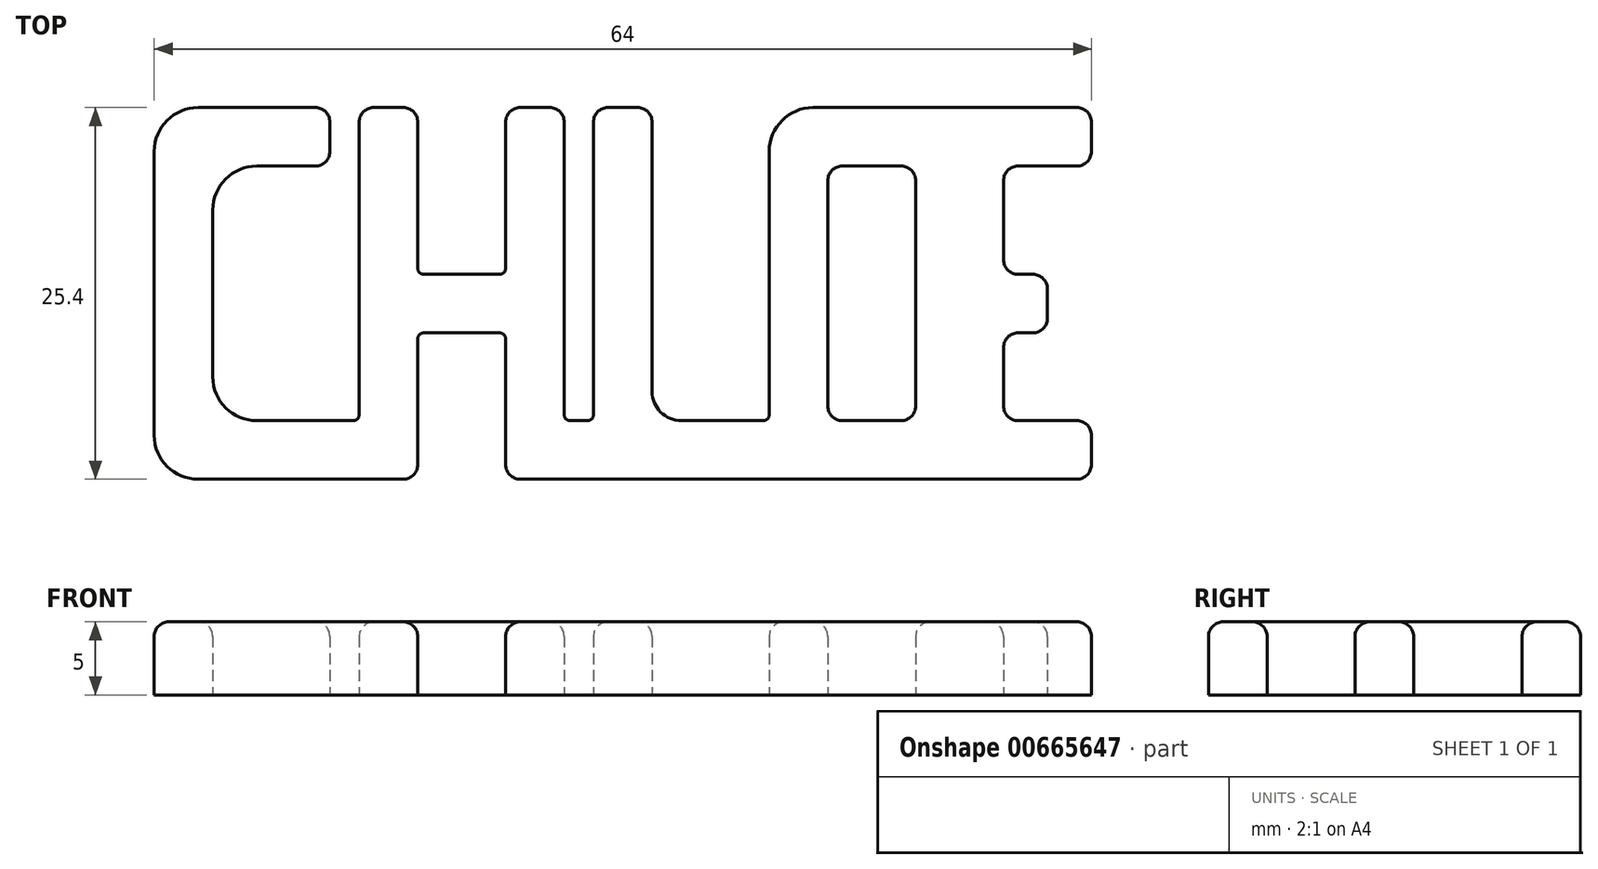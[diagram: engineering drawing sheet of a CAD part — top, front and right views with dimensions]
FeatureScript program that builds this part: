
annotation { "Feature Type Name" : "Feature", "Feature Type Description" : "" }
export const myFeature = defineFeature(function(context is Context, id is Id, definition is map)
    precondition{}
    {
        {
            var Q0;
            Q0=qCreatedBy(makeId("Top.planeOp"),FACE);
            var sketch = newSketch(context, id + "F0", { "sketchPlane" : qUnion([Q0])});
            skLineSegment(sketch, "E0", {"start": v(0, 0) * mm, "end": v(0, 25.4) * mm});
            skLineSegment(sketch, "E1", {"start": v(0, 25.4) * mm, "end": v(12, 25.4) * mm});
            skLineSegment(sketch, "E2", {"start": v(12, 25.4) * mm, "end": v(12, 21.4) * mm});
            skLineSegment(sketch, "E3", {"start": v(12, 21.4) * mm, "end": v(4, 21.4) * mm});
            skLineSegment(sketch, "E4", {"start": v(4, 21.4) * mm, "end": v(4, 4) * mm});
            skLineSegment(sketch, "E5", {"start": v(4, 4) * mm, "end": v(14, 4) * mm});
            skLineSegment(sketch, "E6", {"start": v(14, 4) * mm, "end": v(14, 25.4) * mm});
            skLineSegment(sketch, "E7", {"start": v(14, 25.4) * mm, "end": v(18, 25.4) * mm});
            skLineSegment(sketch, "E8", {"start": v(18, 25.4) * mm, "end": v(18, 14) * mm});
            skLineSegment(sketch, "E9", {"start": v(18, 14) * mm, "end": v(24, 14) * mm});
            skLineSegment(sketch, "E10", {"start": v(24, 14) * mm, "end": v(24, 25.4) * mm});
            skLineSegment(sketch, "E11", {"start": v(24, 25.4) * mm, "end": v(28, 25.4) * mm});
            skLineSegment(sketch, "E12", {"start": v(34, 4) * mm, "end": v(42, 4) * mm});
            skLineSegment(sketch, "E13", {"start": v(42, 4) * mm, "end": v(42, 25.4) * mm});
            skLineSegment(sketch, "E14", {"start": v(42, 25.4) * mm, "end": v(64, 25.4) * mm});
            skLineSegment(sketch, "E15", {"start": v(64, 25.4) * mm, "end": v(64, 21.4) * mm});
            skLineSegment(sketch, "E16", {"start": v(64, 21.4) * mm, "end": v(58, 21.4) * mm});
            skLineSegment(sketch, "E17", {"start": v(58, 21.4) * mm, "end": v(58, 14) * mm});
            skLineSegment(sketch, "E18", {"start": v(58, 14) * mm, "end": v(61, 14) * mm});
            skLineSegment(sketch, "E19", {"start": v(61, 14) * mm, "end": v(61, 10) * mm});
            skLineSegment(sketch, "E20", {"start": v(61, 10) * mm, "end": v(58, 10) * mm});
            skLineSegment(sketch, "E21", {"start": v(58, 10) * mm, "end": v(58, 4) * mm});
            skLineSegment(sketch, "E22", {"start": v(58, 4) * mm, "end": v(64, 4) * mm});
            skLineSegment(sketch, "E23", {"start": v(64, 4) * mm, "end": v(64, 0) * mm});
            skLineSegment(sketch, "E24", {"start": v(64, 0) * mm, "end": v(24, 0) * mm});
            skLineSegment(sketch, "E25", {"start": v(18, 0) * mm, "end": v(18, 10) * mm});
            skLineSegment(sketch, "E26", {"start": v(18, 10) * mm, "end": v(24, 10) * mm});
            skLineSegment(sketch, "E27", {"start": v(24, 10) * mm, "end": v(24, 0) * mm});
            skLineSegment(sketch, "E28.trimOffspring", {"start": v(18, 0) * mm, "end": v(0, 0) * mm});
            skLineSegment(sketch, "E29.bottom", {"start": v(46, 21.4) * mm, "end": v(52, 21.4) * mm});
            skLineSegment(sketch, "E29.top", {"start": v(46, 4) * mm, "end": v(52, 4) * mm});
            skLineSegment(sketch, "E29.left", {"start": v(46, 21.4) * mm, "end": v(46, 4) * mm});
            skLineSegment(sketch, "E29.right", {"start": v(52, 21.4) * mm, "end": v(52, 4) * mm});
            skLineSegment(sketch, "E30", {"start": v(28, 25.4) * mm, "end": v(28, 4) * mm});
            skLineSegment(sketch, "E31", {"start": v(28, 4) * mm, "end": v(30, 4) * mm});
            skLineSegment(sketch, "E32", {"start": v(30, 4) * mm, "end": v(30, 25.4) * mm});
            skLineSegment(sketch, "E33", {"start": v(30, 25.4) * mm, "end": v(34, 25.4) * mm});
            skLineSegment(sketch, "E34", {"start": v(34, 25.4) * mm, "end": v(34, 4) * mm});
            skSolve(sketch);
        }
        {
            var Q0;
            Q0=makeQuery(id+"F0.imprint","IMPRINT",FACE,{"disambiguationData":[TD([[makeQuery(id+"F0.imprint","IMPRINT",EDGE,{"derivedFrom":sQuery(id+"F0.wireOp",EDGE,"E0")}),-1.0]])]});
            extrude(context, id + "F1", {"entities" : qUnion([Q0]), "depth" : 5 * mm, "offsetDistance" : 25 * mm});
        }
        {
            var Q0;
            Q0=makeQuery(id+"F1.opExtrude","SWEPT_EDGE",EDGE,{"disambiguationData":[OSD([sQuery(id+"F0.wireOp",EDGE,"E1"),sQuery(id+"F0.wireOp",EDGE,"E2")])]});
            var Q1;
            Q1=makeQuery(id+"F1.opExtrude","SWEPT_EDGE",EDGE,{"disambiguationData":[OSD([sQuery(id+"F0.wireOp",EDGE,"E2"),sQuery(id+"F0.wireOp",EDGE,"E3")])]});
            var Q2;
            Q2=makeQuery(id+"F1.opExtrude","SWEPT_EDGE",EDGE,{"disambiguationData":[OSD([sQuery(id+"F0.wireOp",EDGE,"E6"),sQuery(id+"F0.wireOp",EDGE,"E7")])]});
            var Q3;
            Q3=makeQuery(id+"F1.opExtrude","SWEPT_EDGE",EDGE,{"disambiguationData":[OSD([sQuery(id+"F0.wireOp",EDGE,"E7"),sQuery(id+"F0.wireOp",EDGE,"E8")])]});
            var Q4;
            Q4=makeQuery(id+"F1.opExtrude","SWEPT_EDGE",EDGE,{"disambiguationData":[OSD([sQuery(id+"F0.wireOp",EDGE,"E10"),sQuery(id+"F0.wireOp",EDGE,"E11")])]});
            var Q5;
            Q5=makeQuery(id+"F1.opExtrude","SWEPT_EDGE",EDGE,{"disambiguationData":[OSD([sQuery(id+"F0.wireOp",EDGE,"E11"),sQuery(id+"F0.wireOp",EDGE,"E30")])]});
            var Q6;
            Q6=makeQuery(id+"F1.opExtrude","SWEPT_EDGE",EDGE,{"disambiguationData":[OSD([sQuery(id+"F0.wireOp",EDGE,"E32"),sQuery(id+"F0.wireOp",EDGE,"E33")])]});
            var Q7;
            Q7=makeQuery(id+"F1.opExtrude","SWEPT_EDGE",EDGE,{"disambiguationData":[OSD([sQuery(id+"F0.wireOp",EDGE,"E33"),sQuery(id+"F0.wireOp",EDGE,"E34")])]});
            var Q8;
            Q8=makeQuery(id+"F1.opExtrude","SWEPT_EDGE",EDGE,{"disambiguationData":[OSD([sQuery(id+"F0.wireOp",EDGE,"E14"),sQuery(id+"F0.wireOp",EDGE,"E15")])]});
            var Q9;
            Q9=makeQuery(id+"F1.opExtrude","SWEPT_EDGE",EDGE,{"disambiguationData":[OSD([sQuery(id+"F0.wireOp",EDGE,"E15"),sQuery(id+"F0.wireOp",EDGE,"E16")])]});
            var Q10;
            Q10=makeQuery(id+"F1.opExtrude","SWEPT_EDGE",EDGE,{"disambiguationData":[OSD([sQuery(id+"F0.wireOp",EDGE,"E18"),sQuery(id+"F0.wireOp",EDGE,"E19")])]});
            var Q11;
            Q11=makeQuery(id+"F1.opExtrude","SWEPT_EDGE",EDGE,{"disambiguationData":[OSD([sQuery(id+"F0.wireOp",EDGE,"E19"),sQuery(id+"F0.wireOp",EDGE,"E20")])]});
            var Q12;
            Q12=makeQuery(id+"F1.opExtrude","SWEPT_EDGE",EDGE,{"disambiguationData":[OSD([sQuery(id+"F0.wireOp",EDGE,"E22"),sQuery(id+"F0.wireOp",EDGE,"E23")])]});
            var Q13;
            Q13=makeQuery(id+"F1.opExtrude","SWEPT_EDGE",EDGE,{"disambiguationData":[OSD([sQuery(id+"F0.wireOp",EDGE,"E23"),sQuery(id+"F0.wireOp",EDGE,"E24")])]});
            var Q14;
            Q14=makeQuery(id+"F1.opExtrude","SWEPT_EDGE",EDGE,{"disambiguationData":[OSD([sQuery(id+"F0.wireOp",EDGE,"E25"),sQuery(id+"F0.wireOp",EDGE,"E28.trimOffspring")])]});
            var Q15;
            Q15=makeQuery(id+"F1.opExtrude","SWEPT_EDGE",EDGE,{"disambiguationData":[OSD([sQuery(id+"F0.wireOp",EDGE,"E24"),sQuery(id+"F0.wireOp",EDGE,"E27")])]});
            var Q16;
            Q16=makeQuery(id+"F1.opExtrude","SWEPT_EDGE",EDGE,{"disambiguationData":[OSD([sQuery(id+"F0.wireOp",EDGE,"E29.bottom"),sQuery(id+"F0.wireOp",EDGE,"E29.left")])]});
            var Q17;
            Q17=makeQuery(id+"F1.opExtrude","SWEPT_EDGE",EDGE,{"disambiguationData":[OSD([sQuery(id+"F0.wireOp",EDGE,"E29.bottom"),sQuery(id+"F0.wireOp",EDGE,"E29.right")])]});
            var Q18;
            Q18=makeQuery(id+"F1.opExtrude","SWEPT_EDGE",EDGE,{"disambiguationData":[OSD([sQuery(id+"F0.wireOp",EDGE,"E29.top"),sQuery(id+"F0.wireOp",EDGE,"E29.right")])]});
            var Q19;
            Q19=makeQuery(id+"F1.opExtrude","SWEPT_EDGE",EDGE,{"disambiguationData":[OSD([sQuery(id+"F0.wireOp",EDGE,"E29.top"),sQuery(id+"F0.wireOp",EDGE,"E29.left")])]});
            fillet(context, id + "F2", {"entities" : qUnion([Q0, Q1, Q2, Q3, Q4, Q5, Q6, Q7, Q8, Q9, Q10, Q11, Q12, Q13, Q14, Q15, Q16, Q17, Q18, Q19]), "tangentPropagation" : true, "radius" : 1 * mm, "defaultsChanged" : false, "vertexSettings" : [], "allowEdgeOverflow" : false});
        }
        {
            var Q0;
            Q0=makeQuery(id+"F1.opExtrude","SWEPT_EDGE",EDGE,{"disambiguationData":[OSD([sQuery(id+"F0.wireOp",EDGE,"E12"),sQuery(id+"F0.wireOp",EDGE,"E34")])]});
            fillet(context, id + "F3", {"entities" : qUnion([Q0]), "tangentPropagation" : true, "radius" : 2 * mm, "defaultsChanged" : false, "vertexSettings" : [], "allowEdgeOverflow" : false});
        }
        {
            var Q0;
            Q0=makeQuery(id+"F1.opExtrude","SWEPT_EDGE",EDGE,{"disambiguationData":[OSD([sQuery(id+"F0.wireOp",EDGE,"E16"),sQuery(id+"F0.wireOp",EDGE,"E17")])]});
            var Q1;
            Q1=makeQuery(id+"F1.opExtrude","SWEPT_EDGE",EDGE,{"disambiguationData":[OSD([sQuery(id+"F0.wireOp",EDGE,"E17"),sQuery(id+"F0.wireOp",EDGE,"E18")])]});
            var Q2;
            Q2=makeQuery(id+"F1.opExtrude","SWEPT_EDGE",EDGE,{"disambiguationData":[OSD([sQuery(id+"F0.wireOp",EDGE,"E20"),sQuery(id+"F0.wireOp",EDGE,"E21")])]});
            var Q3;
            Q3=makeQuery(id+"F1.opExtrude","SWEPT_EDGE",EDGE,{"disambiguationData":[OSD([sQuery(id+"F0.wireOp",EDGE,"E21"),sQuery(id+"F0.wireOp",EDGE,"E22")])]});
            fillet(context, id + "F4", {"entities" : qUnion([Q0, Q1, Q2, Q3]), "tangentPropagation" : true, "radius" : 1 * mm, "defaultsChanged" : false, "vertexSettings" : [], "allowEdgeOverflow" : false});
        }
        {
            var Q0;
            Q0=makeQuery(id+"F1.opExtrude","SWEPT_EDGE",EDGE,{"disambiguationData":[OSD([sQuery(id+"F0.wireOp",EDGE,"E8"),sQuery(id+"F0.wireOp",EDGE,"E9")])]});
            var Q1;
            Q1=makeQuery(id+"F1.opExtrude","SWEPT_EDGE",EDGE,{"disambiguationData":[OSD([sQuery(id+"F0.wireOp",EDGE,"E9"),sQuery(id+"F0.wireOp",EDGE,"E10")])]});
            var Q2;
            Q2=makeQuery(id+"F1.opExtrude","SWEPT_EDGE",EDGE,{"disambiguationData":[OSD([sQuery(id+"F0.wireOp",EDGE,"E26"),sQuery(id+"F0.wireOp",EDGE,"E27")])]});
            var Q3;
            Q3=makeQuery(id+"F1.opExtrude","SWEPT_EDGE",EDGE,{"disambiguationData":[OSD([sQuery(id+"F0.wireOp",EDGE,"E25"),sQuery(id+"F0.wireOp",EDGE,"E26")])]});
            var Q4;
            Q4=makeQuery(id+"F1.opExtrude","SWEPT_EDGE",EDGE,{"disambiguationData":[OSD([sQuery(id+"F0.wireOp",EDGE,"E30"),sQuery(id+"F0.wireOp",EDGE,"E31")])]});
            var Q5;
            Q5=makeQuery(id+"F1.opExtrude","SWEPT_EDGE",EDGE,{"disambiguationData":[OSD([sQuery(id+"F0.wireOp",EDGE,"E31"),sQuery(id+"F0.wireOp",EDGE,"E32")])]});
            var Q6;
            Q6=makeQuery(id+"F1.opExtrude","SWEPT_EDGE",EDGE,{"disambiguationData":[OSD([sQuery(id+"F0.wireOp",EDGE,"E12"),sQuery(id+"F0.wireOp",EDGE,"E13")])]});
            var Q7;
            Q7=makeQuery(id+"F1.opExtrude","SWEPT_EDGE",EDGE,{"disambiguationData":[OSD([sQuery(id+"F0.wireOp",EDGE,"E5"),sQuery(id+"F0.wireOp",EDGE,"E6")])]});
            fillet(context, id + "F5", {"entities" : qUnion([Q0, Q1, Q2, Q3, Q4, Q5, Q6, Q7]), "tangentPropagation" : true, "radius" : 0.4 * mm, "defaultsChanged" : false, "vertexSettings" : [], "allowEdgeOverflow" : false});
        }
        {
            var Q0;
            Q0=makeQuery(id+"F1.opExtrude","SWEPT_EDGE",EDGE,{"disambiguationData":[OSD([sQuery(id+"F0.wireOp",EDGE,"E3"),sQuery(id+"F0.wireOp",EDGE,"E4")])]});
            var Q1;
            Q1=makeQuery(id+"F1.opExtrude","SWEPT_EDGE",EDGE,{"disambiguationData":[OSD([sQuery(id+"F0.wireOp",EDGE,"E4"),sQuery(id+"F0.wireOp",EDGE,"E5")])]});
            var Q2;
            Q2=makeQuery(id+"F1.opExtrude","SWEPT_EDGE",EDGE,{"disambiguationData":[OSD([sQuery(id+"F0.wireOp",EDGE,"E0"),sQuery(id+"F0.wireOp",EDGE,"E1")])]});
            var Q3;
            Q3=makeQuery(id+"F1.opExtrude","SWEPT_EDGE",EDGE,{"disambiguationData":[OSD([sQuery(id+"F0.wireOp",EDGE,"E0"),sQuery(id+"F0.wireOp",EDGE,"E28.trimOffspring")])]});
            var Q4;
            Q4=makeQuery(id+"F1.opExtrude","SWEPT_EDGE",EDGE,{"disambiguationData":[OSD([sQuery(id+"F0.wireOp",EDGE,"E13"),sQuery(id+"F0.wireOp",EDGE,"E14")])]});
            fillet(context, id + "F6", {"entities" : qUnion([Q0, Q1, Q2, Q3, Q4]), "tangentPropagation" : true, "radius" : 3 * mm, "defaultsChanged" : false, "vertexSettings" : [], "allowEdgeOverflow" : false});
        }
        {
            var Q0;
            Q0=makeQuery(id+"F1.opExtrude","CAP_FACE",FACE,{"disambiguationData":[OSD([sQuery(id+"F0.wireOp",EDGE,"E0"),sQuery(id+"F0.wireOp",EDGE,"E1"),sQuery(id+"F0.wireOp",EDGE,"E2"),sQuery(id+"F0.wireOp",EDGE,"E3"),sQuery(id+"F0.wireOp",EDGE,"E4"),sQuery(id+"F0.wireOp",EDGE,"E5"),sQuery(id+"F0.wireOp",EDGE,"E6"),sQuery(id+"F0.wireOp",EDGE,"E7"),sQuery(id+"F0.wireOp",EDGE,"E8"),sQuery(id+"F0.wireOp",EDGE,"E9"),sQuery(id+"F0.wireOp",EDGE,"E10"),sQuery(id+"F0.wireOp",EDGE,"E11"),sQuery(id+"F0.wireOp",EDGE,"E12"),sQuery(id+"F0.wireOp",EDGE,"E13"),sQuery(id+"F0.wireOp",EDGE,"E14"),sQuery(id+"F0.wireOp",EDGE,"E15"),sQuery(id+"F0.wireOp",EDGE,"E16"),sQuery(id+"F0.wireOp",EDGE,"E17"),sQuery(id+"F0.wireOp",EDGE,"E18"),sQuery(id+"F0.wireOp",EDGE,"E19"),sQuery(id+"F0.wireOp",EDGE,"E20"),sQuery(id+"F0.wireOp",EDGE,"E21"),sQuery(id+"F0.wireOp",EDGE,"E22"),sQuery(id+"F0.wireOp",EDGE,"E23"),sQuery(id+"F0.wireOp",EDGE,"E24"),sQuery(id+"F0.wireOp",EDGE,"E25"),sQuery(id+"F0.wireOp",EDGE,"E26"),sQuery(id+"F0.wireOp",EDGE,"E27"),sQuery(id+"F0.wireOp",EDGE,"E28.trimOffspring"),sQuery(id+"F0.wireOp",EDGE,"E29.bottom"),sQuery(id+"F0.wireOp",EDGE,"E29.top"),sQuery(id+"F0.wireOp",EDGE,"E29.left"),sQuery(id+"F0.wireOp",EDGE,"E29.right"),sQuery(id+"F0.wireOp",EDGE,"E30"),sQuery(id+"F0.wireOp",EDGE,"E31"),sQuery(id+"F0.wireOp",EDGE,"E32"),sQuery(id+"F0.wireOp",EDGE,"E33"),sQuery(id+"F0.wireOp",EDGE,"E34")])],"isStart":false});
            fillet(context, id + "F7", {"entities" : qUnion([Q0]), "tangentPropagation" : true, "radius" : 1 * mm, "defaultsChanged" : true, "vertexSettings" : [], "allowEdgeOverflow" : false});
        }
    });
